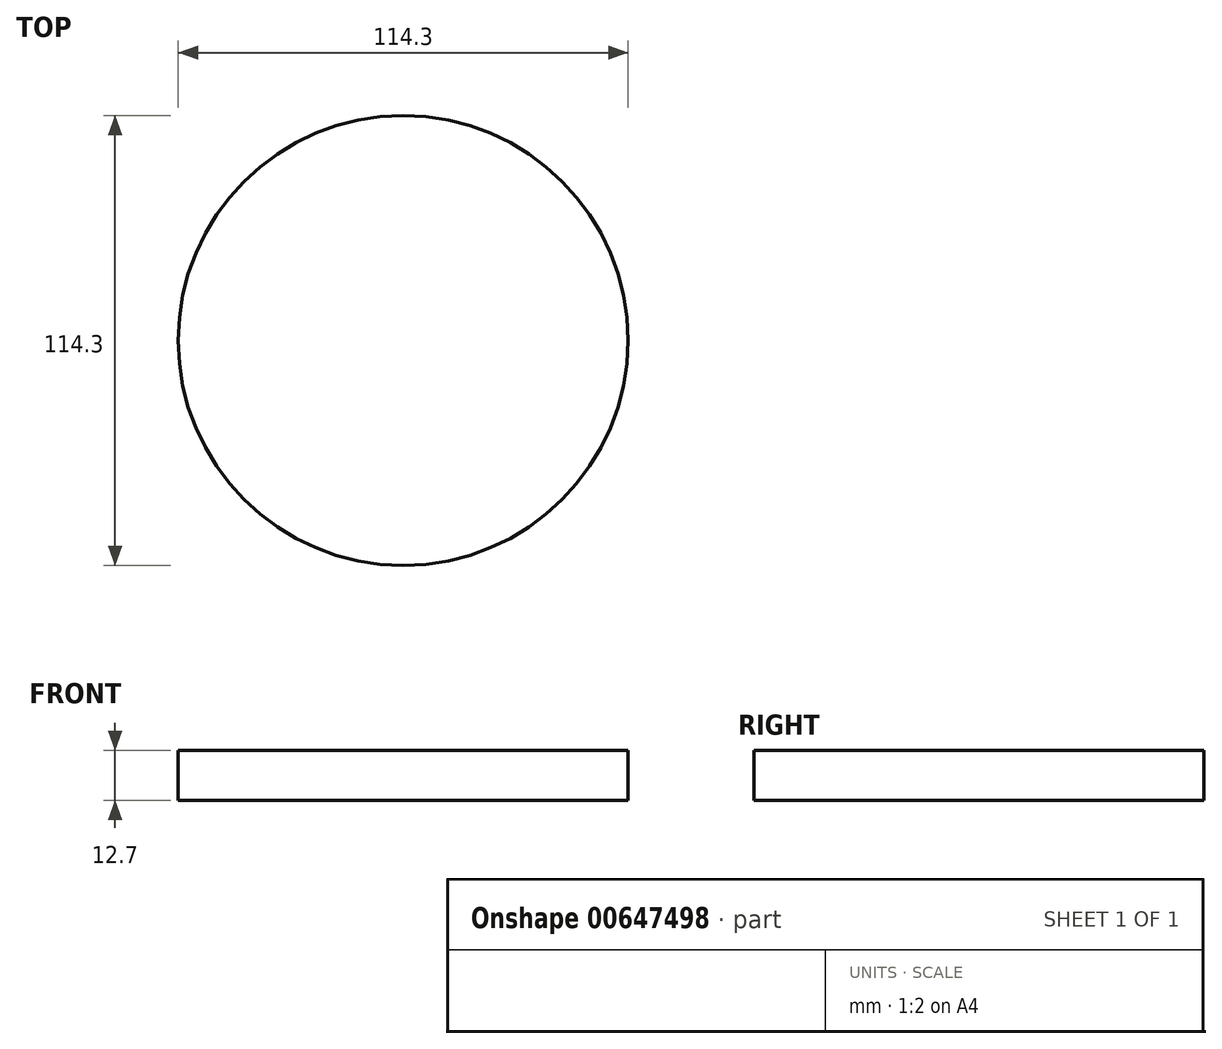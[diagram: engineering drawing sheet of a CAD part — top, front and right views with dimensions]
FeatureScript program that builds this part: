
annotation { "Feature Type Name" : "Feature", "Feature Type Description" : "" }
export const myFeature = defineFeature(function(context is Context, id is Id, definition is map)
    precondition{}
    {
        {
            var Q0;
            Q0=qCreatedBy(makeId("Top.planeOp"),FACE);
            var sketch = newSketch(context, id + "F0", { "sketchPlane" : qUnion([Q0])});
            skCircle(sketch, "E0", {"center": v(0, 0) * mm, "radius": 57.15 * mm});
            skSolve(sketch);
        }
        {
            var Q0;
            Q0=qSketchRegion(id+"F0",true);
            extrude(context, id + "F1", {"entities" : qUnion([Q0]), "depth" : 12.7 * mm});
        }
    });
